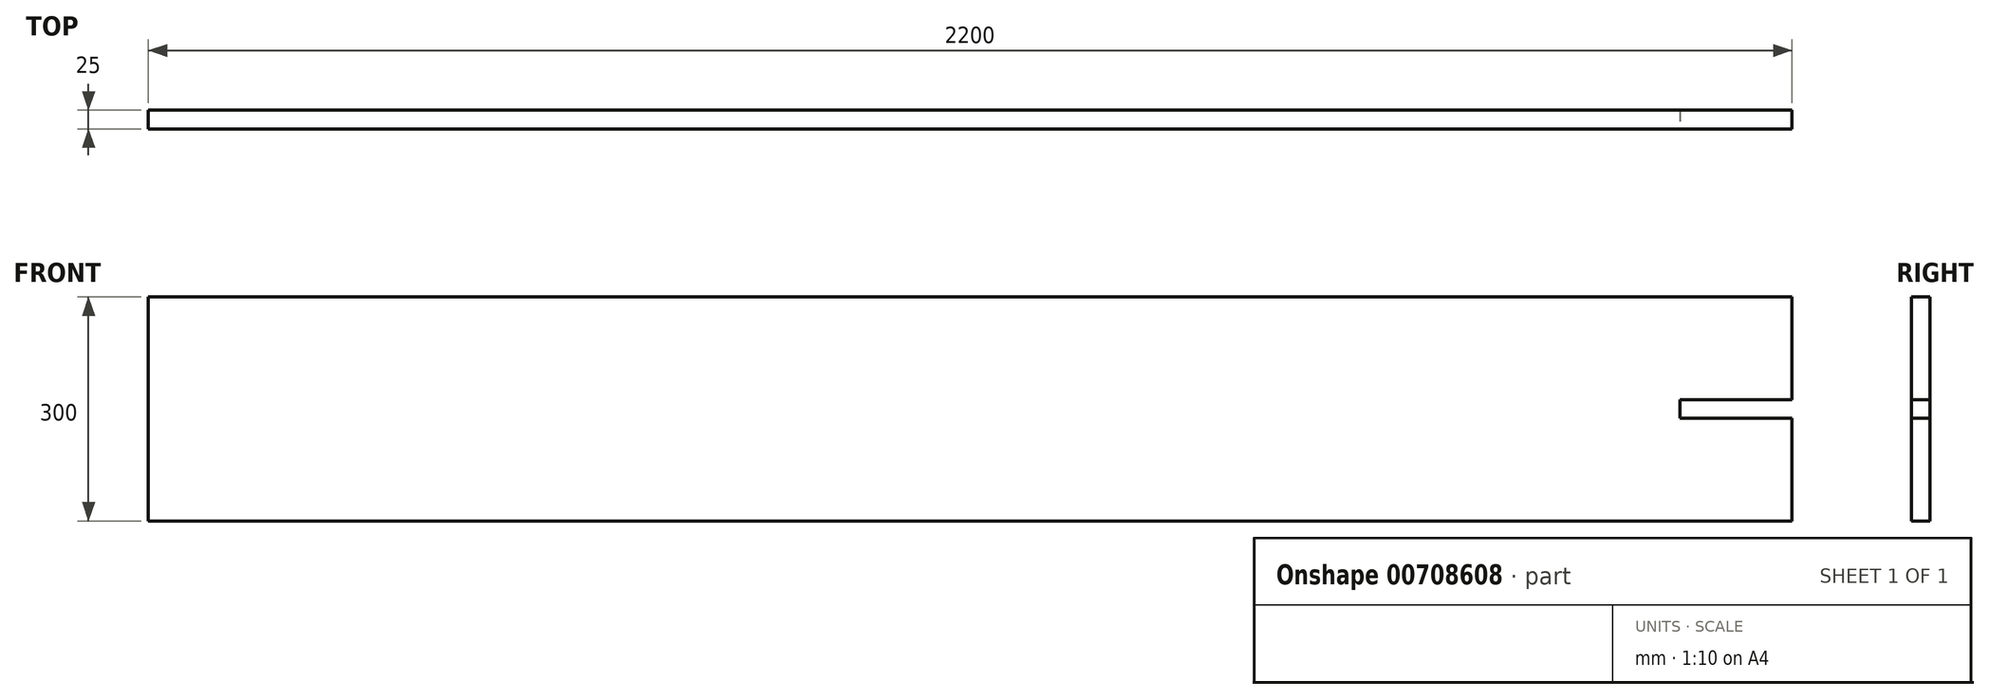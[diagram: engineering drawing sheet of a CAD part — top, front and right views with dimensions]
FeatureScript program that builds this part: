
annotation { "Feature Type Name" : "Feature", "Feature Type Description" : "" }
export const myFeature = defineFeature(function(context is Context, id is Id, definition is map)
    precondition{}
    {
        {
            var Q0;
            Q0=qCreatedBy(makeId("Front.planeOp"),FACE);
            var sketch = newSketch(context, id + "F0", { "sketchPlane" : qUnion([Q0])});
            skLineSegment(sketch, "E0.bottom", {"start": v(0, 0) * mm, "end": v(2200, 0) * mm});
            skLineSegment(sketch, "E0.top", {"start": v(0, 300) * mm, "end": v(2200, 300) * mm});
            skLineSegment(sketch, "E0.left", {"start": v(0, 0) * mm, "end": v(0, 300) * mm});
            skLineSegment(sketch, "E0.right", {"start": v(2200, 0) * mm, "end": v(2200, 300) * mm});
            skSolve(sketch);
        }
        {
            var Q0;
            Q0=makeQuery(id+"F0.imprint","IMPRINT",FACE,{"disambiguationData":[TD([[makeQuery(id+"F0.imprint","IMPRINT",EDGE,{"derivedFrom":sQuery(id+"F0.wireOp",EDGE,"E0.bottom")}),1.0]])]});
            extrude(context, id + "F1", {"entities" : qUnion([Q0]), "depth" : 25 * mm, "offsetDistance" : 25 * mm});
        }
        {
            var Q0;
            Q0=makeQuery(id+"F1.opExtrude","CAP_FACE",FACE,{"disambiguationData":[OSD([sQuery(id+"F0.wireOp",EDGE,"E0.bottom"),sQuery(id+"F0.wireOp",EDGE,"E0.top"),sQuery(id+"F0.wireOp",EDGE,"E0.left"),sQuery(id+"F0.wireOp",EDGE,"E0.right")])],"isStart":false});
            var sketch = newSketch(context, id + "F2", { "sketchPlane" : qUnion([Q0])});
            skLineSegment(sketch, "E1.bottom", {"start": v(2350, 162.5) * mm, "end": v(2050, 162.5) * mm});
            skLineSegment(sketch, "E1.top", {"start": v(2350, 137.5) * mm, "end": v(2050, 137.5) * mm});
            skLineSegment(sketch, "E1.left", {"start": v(2350, 162.5) * mm, "end": v(2350, 137.5) * mm});
            skLineSegment(sketch, "E1.right", {"start": v(2050, 162.5) * mm, "end": v(2050, 137.5) * mm});
            skPoint(sketch, "E1.middle", {"position": v(2200, 150) * mm});
            skSolve(sketch);
        }
        {
            var Q0;
            {var subQ0=sQuery(id+"F2.wireOp",EDGE,"E1.right");Q0=makeQuery(id+"F2.imprint","IMPRINT",FACE,{"disambiguationData":[TD([[makeQuery(id+"F2.imprint","IMPRINT",EDGE,{"derivedFrom":subQ0}),1.0]])]});}
            extrude(context, id + "F3", {"entities" : qUnion([Q0]), "operationType" : NewBodyOperationType.REMOVE, "endBound" : BoundingType.THROUGH_ALL, "oppositeDirection" : true, "depth" : 25 * mm, "offsetDistance" : 25 * mm});
        }
    });
